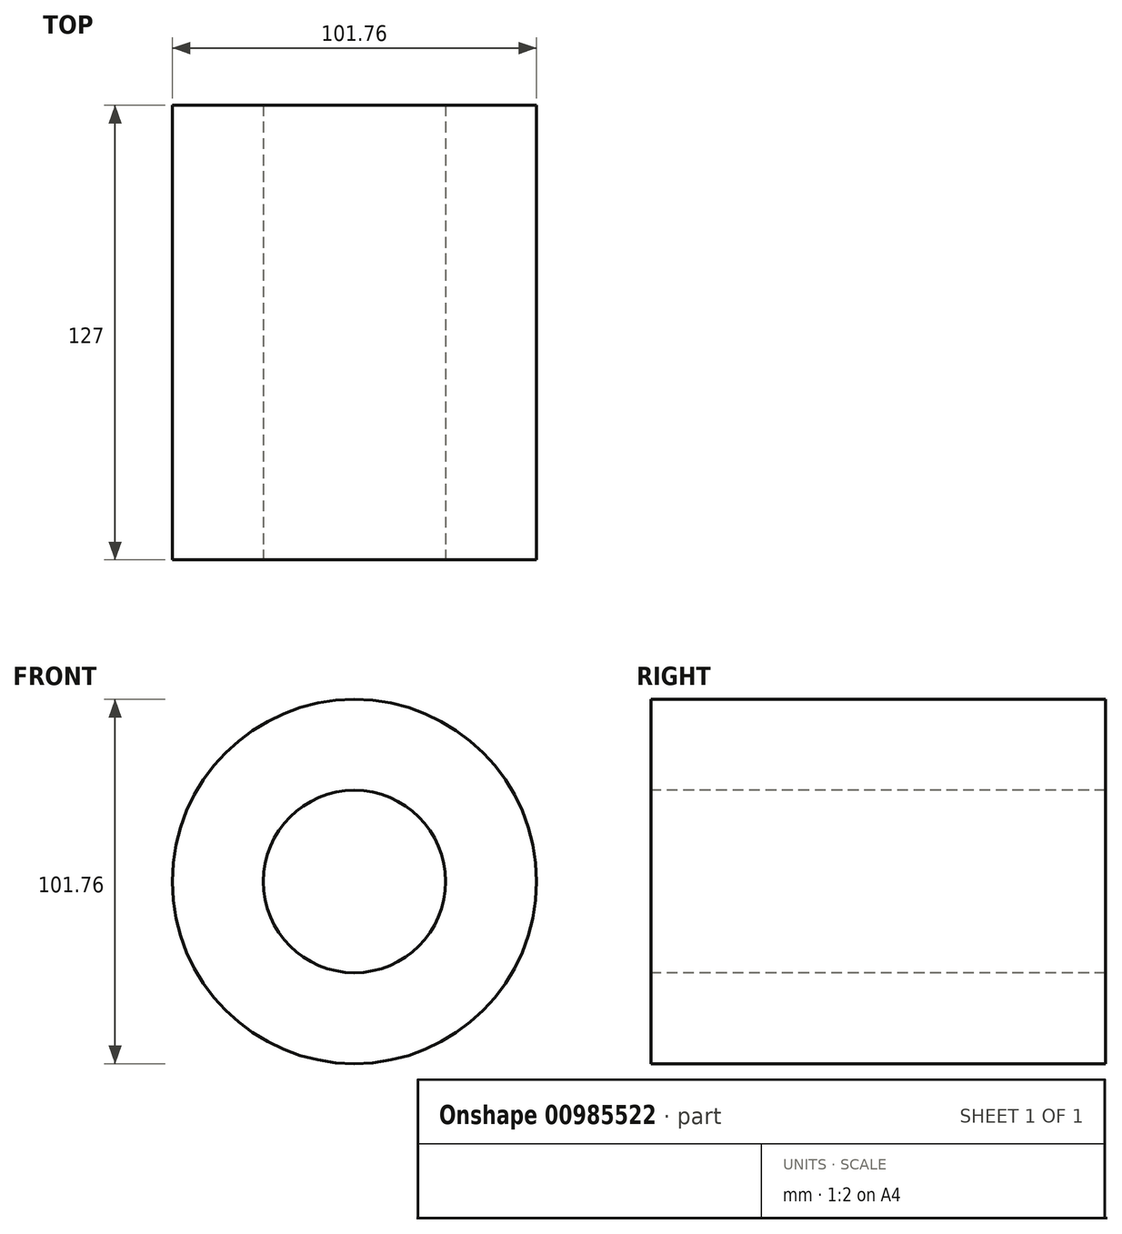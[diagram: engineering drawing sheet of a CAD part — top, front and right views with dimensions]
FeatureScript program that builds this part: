
annotation { "Feature Type Name" : "Feature", "Feature Type Description" : "" }
export const myFeature = defineFeature(function(context is Context, id is Id, definition is map)
    precondition{}
    {
        {
            var Q0;
            Q0=qCreatedBy(makeId("Front.planeOp"),FACE);
            var sketch = newSketch(context, id + "F0", { "sketchPlane" : qUnion([Q0])});
            skCircle(sketch, "E0", {"center": v(0, 0) * mm, "radius": 50.88 * mm});
            skCircle(sketch, "E1", {"center": v(0, 0) * mm, "radius": 25.48 * mm});
            skSolve(sketch);
        }
        {
            var Q0;
            Q0=makeQuery(id+"F0.imprint","IMPRINT",FACE,{"disambiguationData":[TD([[makeQuery(id+"F0.imprint","IMPRINT",EDGE,{"derivedFrom":sQuery(id+"F0.wireOp",EDGE,"E0")}),1.0]])]});
            extrude(context, id + "F1", {"entities" : qUnion([Q0]), "oppositeDirection" : true, "depth" : 127 * mm, "offsetDistance" : 25.4 * mm});
        }
    });
